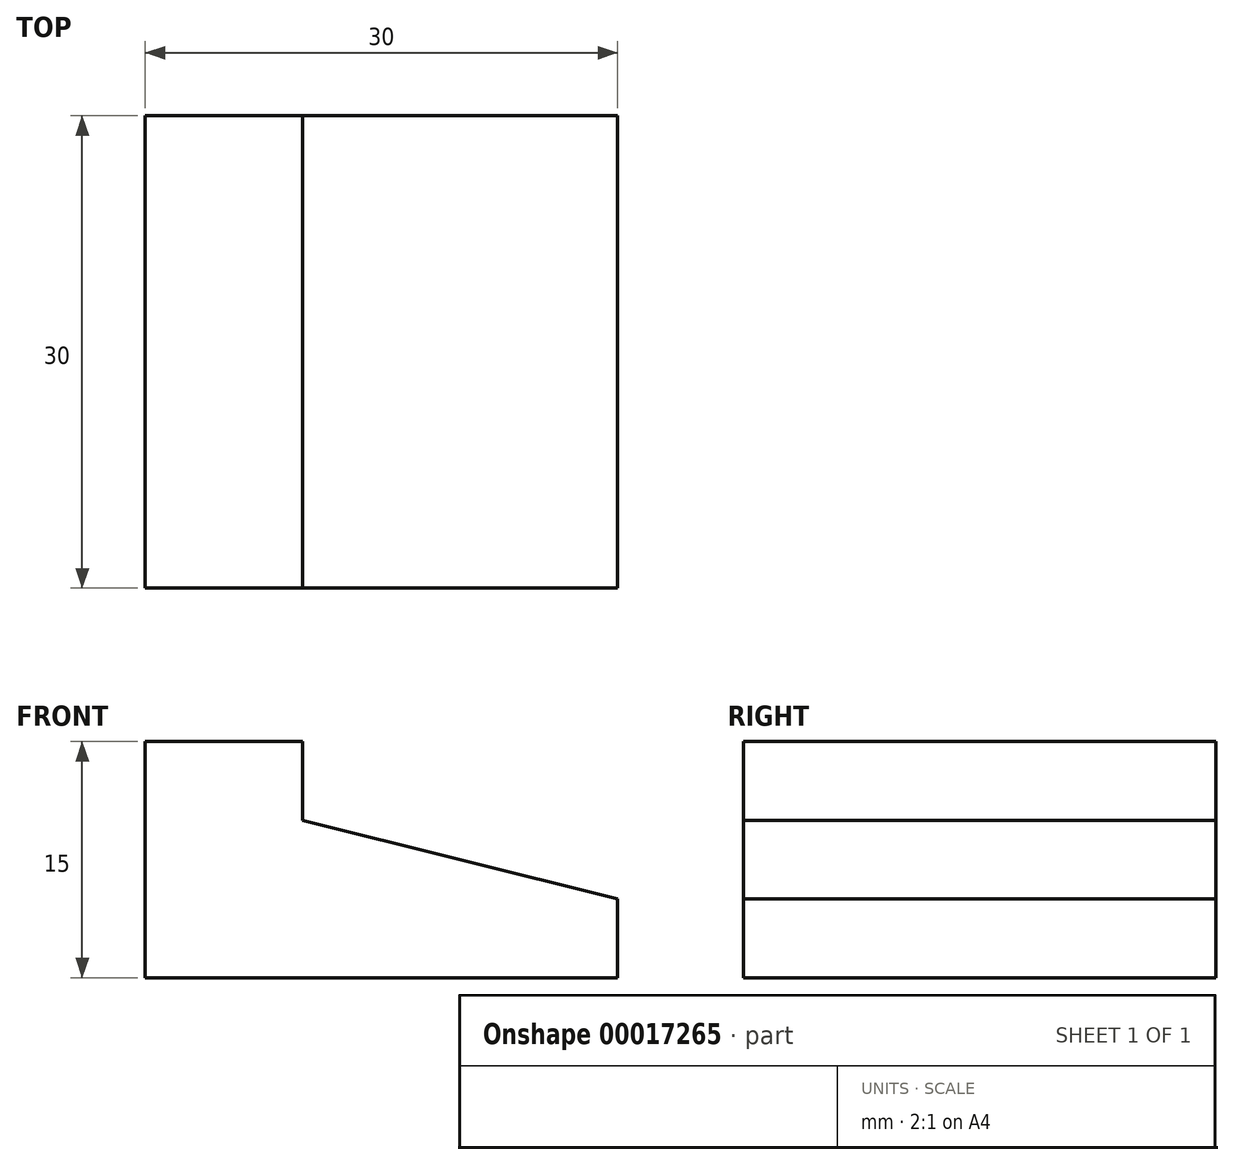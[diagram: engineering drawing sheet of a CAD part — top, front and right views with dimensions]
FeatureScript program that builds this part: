
annotation { "Feature Type Name" : "Feature", "Feature Type Description" : "" }
export const myFeature = defineFeature(function(context is Context, id is Id, definition is map)
    precondition{}
    {
        {
            var Q0;
            Q0=qCreatedBy(makeId("Front.planeOp"),FACE);
            var sketch = newSketch(context, id + "F0", { "sketchPlane" : qUnion([Q0])});
            skLineSegment(sketch, "E0", {"start": v(-30.4, 40.87) * mm, "end": v(-30.4, 25.87) * mm});
            skLineSegment(sketch, "E1", {"start": v(-30.4, 25.87) * mm, "end": v(-0.4, 25.87) * mm});
            skLineSegment(sketch, "E2", {"start": v(-0.4, 25.87) * mm, "end": v(-0.4, 30.87) * mm});
            skLineSegment(sketch, "E3", {"start": v(-0.4, 30.87) * mm, "end": v(-20.4, 35.87) * mm});
            skLineSegment(sketch, "E4", {"start": v(-20.4, 35.87) * mm, "end": v(-20.4, 40.87) * mm});
            skLineSegment(sketch, "E5", {"start": v(-20.4, 40.87) * mm, "end": v(-30.4, 40.87) * mm});
            skSolve(sketch);
        }
        {
            var Q0;
            Q0 = qSketchRegion(id + "F0", true);
            extrude(context, id + "F1", {"entities" : qUnion([Q0]), "depth" : 30 * mm});
        }
    });
